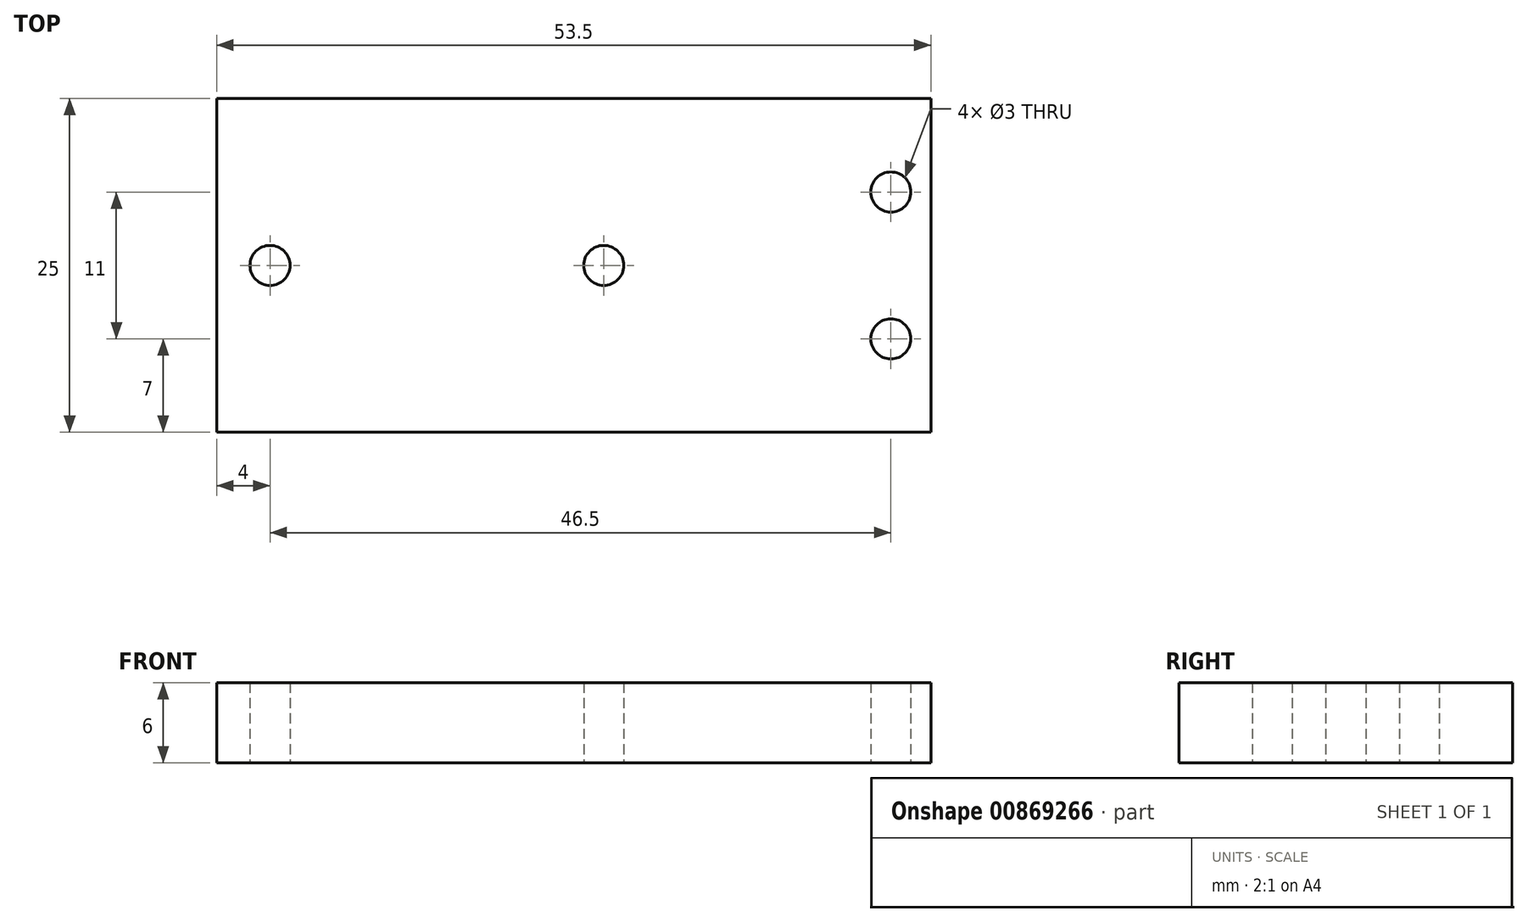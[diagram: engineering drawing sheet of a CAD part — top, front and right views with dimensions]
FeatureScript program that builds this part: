
annotation { "Feature Type Name" : "Feature", "Feature Type Description" : "" }
export const myFeature = defineFeature(function(context is Context, id is Id, definition is map)
    precondition{}
    {
        {
            var Q0;
            Q0=qCreatedBy(makeId("Top.planeOp"),FACE);
            var sketch = newSketch(context, id + "F0", { "sketchPlane" : qUnion([Q0])});
            skLineSegment(sketch, "E0.bottom", {"start": v(27.5, 12.5) * mm, "end": v(-27.5, 12.5) * mm});
            skLineSegment(sketch, "E0.top", {"start": v(27.5, -12.5) * mm, "end": v(-27.5, -12.5) * mm});
            skLineSegment(sketch, "E0.left", {"start": v(27.5, 12.5) * mm, "end": v(27.5, -12.5) * mm});
            skLineSegment(sketch, "E0.right", {"start": v(-27.5, 12.5) * mm, "end": v(-27.5, -12.5) * mm});
            skPoint(sketch, "E0.middle", {"position": v(0, 0) * mm});
            skLineSegment(sketch, "E1.right", {"start": v(23, -5.5) * mm, "end": v(23, 5.5) * mm});
            skLineSegment(sketch, "E2", {"start": v(23, 0) * mm, "end": v(1.5, 0) * mm});
            skLineSegment(sketch, "E3", {"start": v(1.5, 0) * mm, "end": v(-23.5, 0) * mm});
            skSolve(sketch);
        }
        {
            var Q0;
            Q0=makeQuery(id+"F0.imprint","IMPRINT",FACE,{"disambiguationData":[TD([[makeQuery(id+"F0.imprint","IMPRINT",EDGE,{"derivedFrom":sQuery(id+"F0.wireOp",EDGE,"E0.bottom")}),1.0]])]});
            var Q1;
            Q1=makeQuery(id+"F0.imprint","IMPRINT",FACE,{"disambiguationData":[TD([[makeQuery(id+"F0.imprint","IMPRINT",EDGE,{"derivedFrom":sQuery(id+"F0.wireOp",EDGE,"E1.bottom")}),-1.0]])]});
            extrude(context, id + "F1", {"entities" : qUnion([Q0, Q1]), "depth" : 6 * mm, "offsetDistance" : 25 * mm});
        }
        {
            var Q0;
            Q0=sQuery(id+"F0.wireOp",VERTEX,"E1.top.end");
            var Q1;
            Q1=sQuery(id+"F0.wireOp",VERTEX,"E1.bottom.end");
            var Q2;
            Q2=sQuery(id+"F0.wireOp",VERTEX,"E1.top.start");
            var Q3;
            Q3=sQuery(id+"F0.wireOp",VERTEX,"E1.bottom.start");
            var Q4;
            Q4=sQuery(id+"F0.wireOp",VERTEX,"JNorPfZ4-P7x9-lvs2-xDjA-NJwynsm60dqW.end");
            var Q5;
            Q5=sQuery(id+"F0.wireOp",VERTEX,"E3.end");
            var Q6;
            Q6=sQuery(id+"F0.wireOp",VERTEX,"E1.right.end");
            var Q7;
            Q7=sQuery(id+"F0.wireOp",VERTEX,"E1.right.start");
            var Q8;
            Q8=sQuery(id+"F0.wireOp",VERTEX,"E2.end");
            var Q9;
            Q9=makeQuery(id+"F1.opExtrude","SWEPT_BODY",BODY,{"disambiguationData":[OSD([sQuery(id+"F0.wireOp",EDGE,"E0.bottom"),sQuery(id+"F0.wireOp",EDGE,"E0.top"),sQuery(id+"F0.wireOp",EDGE,"E0.left"),sQuery(id+"F0.wireOp",EDGE,"E0.right")])]});
            hole(context, id + "F2", {"style" : HoleStyle.SIMPLE, "endStyle" : HoleEndStyle.THROUGH, "oppositeDirection" : true, "holeDiameter" : 3 * mm, "majorDiameter" : 5 * mm, "isTappedThrough" : true, "tappedDepth" : 12 * mm, "tapClearance" : 3, "locations" : qUnion([Q0, Q1, Q2, Q3, Q4, Q5, Q6, Q7, Q8]), "scope" : qUnion([Q9])});
        }
        {
            var Q0;
            Q0=makeQuery(id+"F1.opExtrude","SWEPT_FACE",FACE,{"disambiguationData":[OSD([sQuery(id+"F0.wireOp",EDGE,"E0.left")])]});
            extrude(context, id + "F3", {"entities" : qUnion([Q0]), "operationType" : NewBodyOperationType.REMOVE, "oppositeDirection" : true, "depth" : 1.5 * mm, "offsetDistance" : 25 * mm});
        }
    });
